# Revit family: Door_Access_Drywall-Recess_Acudor_DW-5058
name_source: partatom
category: Generic Models
units: mm (PartAtom-declared; Revit-internal decimal feet)

## family parameters
Can host rebar = No
Cut with Voids When Loaded = No
Host = Face
Part Type = Normal
Room Calculation Point = No
Round Connector Dimension = Use Diameter
Shared = No

## types (5) — shared parameters
Default Elevation = 0' - 0"
Description = Acudor Recessed Drywall Panel Access Door for Wall or Ceiling - DW-5058 as Specified
Fire Performance = as Specified
Green Building-LEED = http://www.arcat.com
Manufacturer = Acudor Products Inc
Manufacturer Fax = 973-575-5160
Manufacturer Website = http://www.acudor.com
Model = DW-5058
Product Data = http://www.arcat.com
Revision = R1_2017-03
Sales Information = http://www.acudor.com
Standards Conformance = as Specified
URL = http://www.acudor.com
Unit Depth = 0' - 1 1/2"
zero-valued in all types: Expected Lifespan (Years), Maintenance Schedule (Months), Warranty Duration (Years)

## per-type parameters (varying)
| type | Clear Opening Height | Clear Opening Width | Door Height | Door Width | Opening Height | Opening Width | Overall Height | Overall Width | Unit Height | Unit Weight | Unit Width |
| 24 x 36 Nom | 3' - 0" | 2' - 0" | 2' - 11 7/8" | 1' - 11 7/8" | 3' - 0 3/8" | 2' - 0 3/8" | 3' - 2" | 2' - 2" | 3' - 0" | 10 | 2' - 0" |
| 24 x 24 Nom | 2' - 0" | 2' - 0" | 1' - 11 7/8" | 1' - 11 7/8" | 2' - 0 3/8" | 2' - 0 3/8" | 2' - 2" | 2' - 2" | 2' - 0" | 6 | 2' - 0" |
| 18 x 18 Nom | 1' - 6" | 1' - 6" | 1' - 5 7/8" | 1' - 5 7/8" | 1' - 6 3/8" | 1' - 6 3/8" | 1' - 8" | 1' - 8" | 1' - 6" | 3 | 1' - 6" |
| 16 x 16 Nom | 1' - 4" | 1' - 4" | 1' - 3 7/8" | 1' - 3 7/8" | 1' - 4 3/8" | 1' - 4 3/8" | 1' - 6" | 1' - 6" | 1' - 4" | 2 | 1' - 4" |
| 12 x 12 Nom | 1' - 0" | 1' - 0" | 0' - 11 7/8" | 0' - 11 7/8" | 1' - 0 3/8" | 1' - 0 3/8" | 1' - 2" | 1' - 2" | 1' - 0" | 1 | 1' - 0" |

## geometry (parser evidence)
native form markers: Sweep x3
no freeform markers — native parametric forms only
